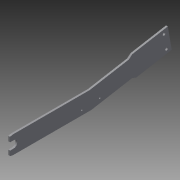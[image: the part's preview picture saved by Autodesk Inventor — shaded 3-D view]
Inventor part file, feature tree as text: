
AUTODESK INVENTOR PART (.ipt)
format: ipt  version: 2013 (Build 170138000, 138)  size: 154,624 bytes
history: native  units: mm
features: sketch x3, other x2, extrude x2, hole x2
ambient origin geometry x8: Origin, YZ Plane, XZ Plane, XY Plane, X Axis, Y Axis, Z Axis, Center Point
feature tree (9):
  other  "ソリッド1"
  extrude  "押し出し1"  Depth=20.0mm
  hole  "穴2"  [1 undecoded]
  extrude  "押し出し2"  Depth=10.0mm
  hole  "穴3"  [1 undecoded]
  sketch  "スケッチ4"
  sketch  "スケッチ5"
  sketch  "スケッチ6"
  other  "断面エッジを投影1"
note: 2 required parameter values undecoded (feature->parameter linkage not recoverable at this tier; creation-order binding heuristic only, values carry confidence <= 0.55)
